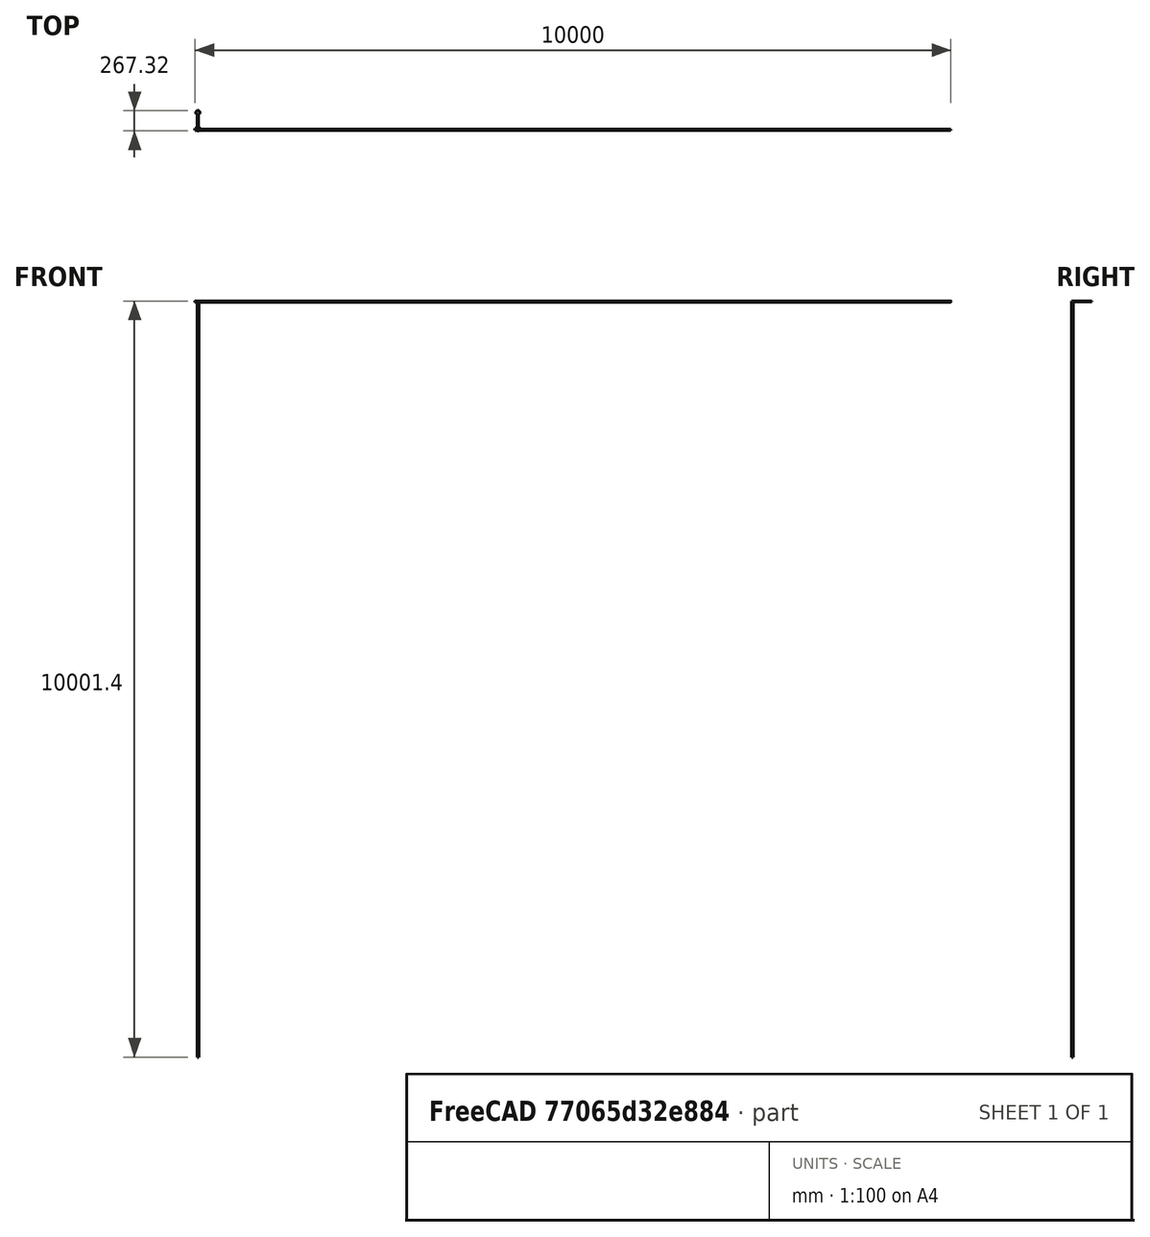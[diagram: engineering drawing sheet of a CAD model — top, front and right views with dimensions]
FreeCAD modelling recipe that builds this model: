
FCSTD DOCUMENT  (FreeCAD 0.16R)
Label: WheelSpacer100mm
License: All rights reserved
LicenseURL: http://en.wikipedia.org/wiki/All_rights_reserved
objects: Sketcher::SketchObject×4, PartDesign::Pocket×3, PartDesign::Chamfer×3, PartDesign::Pad×1, Mesh::Feature×1
note: 15 computed .brp shape members not serialized (recipe doc carries the construction recipe); baked Part::Feature solids carry a one-line shape summary decoded from their .brp

FEATURE [Sketcher::SketchObject] Sketch
  sketch-geometry (9):
    g0: ArcOfCircle CenterX=0 CenterY=227 CenterZ=0 NormalX=0 NormalY=0 NormalZ=1 Radius=25 StartAngle=5.01708 EndAngle=10.6909
    g1: LineSegment [constr] StartX=-40 StartY=252 StartZ=0 EndX=40 EndY=252 EndZ=0
    g2: LineSegment StartX=-7.5 StartY=203.152 StartZ=0 EndX=-7.5 EndY=20 EndZ=0
    g3: LineSegment StartX=7.5 StartY=203.152 StartZ=0 EndX=7.5 EndY=20 EndZ=0
    g4: LineSegment StartX=37.5 StartY=20 StartZ=0 EndX=37.5 EndY=-5 EndZ=0
    g5: LineSegment StartX=37.5 StartY=-5 StartZ=0 EndX=-37.5 EndY=-5 EndZ=0
    g6: LineSegment StartX=-37.5 StartY=-5 StartZ=0 EndX=-37.5 EndY=20 EndZ=0
    g7: LineSegment StartX=-37.5 StartY=20 StartZ=0 EndX=-7.5 EndY=20 EndZ=0
    g8: LineSegment StartX=7.5 StartY=20 StartZ=0 EndX=37.5 EndY=20 EndZ=0
  constraints (28):
    c: Radius(g0) = 25
    c: Tangent(g1,g0)
    c: Horizontal(g1)
    c: Symmetric(g1,g1,g-2)
    c: PointOnObject(g0,g-2)
    c: DistanceY(g1) = 252
    c: Vertical(g2)
    c: Vertical(g3)
    c: Coincident(g4,g5)
    c: Coincident(g5,g6)
    c: Horizontal(g5)
    c: Vertical(g4)
    c: Vertical(g6)
    c: Symmetric(g4,g6,g-2)
    c: Coincident(g7,g6)
    c: Coincident(g7,g2)
    c: Coincident(g8,g3)
    c: Coincident(g8,g4)
    c: Horizontal(g7)
    c: Horizontal(g8)
    c: Distance(g4,g6) = 75
    c: DistanceY(g4) = -5
    c: Coincident(g0,g3)
    c: Coincident(g0,g2)
    c: Symmetric(g0,g0,g-2)
    c: Distance(g0,g0) = 15
    c: DistanceY(g4) = 20
    c: Distance(g1) = 80
FEATURE [PartDesign::Pad] Pad
  Length = 10
  Length2 = 100
  Midplane = true
  Sketch = -> Sketch
  Type = 0
FEATURE [Sketcher::SketchObject] Sketch001
  Placement = pos=(-37.5,0,0) rot=(0.57735,-0.57735,-0.57735;2.0944rad)
  Support = -> Pad [Face5]
  sketch-geometry (1):
    g0: Circle CenterX=0 CenterY=0 CenterZ=0 NormalX=0 NormalY=0 NormalZ=1 Radius=6.35
  constraints (2):
    c: Radius(g0) = 6.35
    c: Coincident(g0,g-1)
FEATURE [PartDesign::Pocket] Pocket
  Length = 5
  Sketch = -> Sketch001
  Type = 1
FEATURE [Sketcher::SketchObject] Sketch002
  Placement = pos=(0,0,5) rot=(0,0,1;0rad)
  Support = -> Pocket [Face5]
  sketch-geometry (3):
    g0: LineSegment StartX=0 StartY=2 StartZ=0 EndX=-10 EndY=-15.3205 EndZ=0
    g1: LineSegment StartX=-10 StartY=-15.3205 StartZ=0 EndX=10 EndY=-15.3205 EndZ=0
    g2: LineSegment StartX=10 StartY=-15.3205 StartZ=0 EndX=0 EndY=2 EndZ=0
  constraints (10):
    c: PointOnObject(g0,g-2)
    c: Coincident(g0,g1)
    c: Horizontal(g1)
    c: Coincident(g1,g2)
    c: Coincident(g2,g0)
    c: DistanceY(g0) = 2
    c: Equal(g2,g0)
    c: Symmetric(g1,g0,g-2)
    c: Distance(g1) = 20
    c: Distance(g2) = 20
FEATURE [PartDesign::Pocket] Pocket001
  Length = 5
  Sketch = -> Sketch002
  Type = 1
FEATURE [Sketcher::SketchObject] Sketch003
  Placement = pos=(0,0,5) rot=(0,0,1;0rad)
  Support = -> Pocket001 [Face5]
  sketch-geometry (3):
    g0: LineSegment StartX=0 StartY=7.0119 StartZ=0 EndX=-10.687 EndY=-5.4526 EndZ=0
    g1: LineSegment StartX=-10.687 StartY=-5.4526 StartZ=0 EndX=10.687 EndY=-5.4526 EndZ=0
    g2: LineSegment StartX=10.687 StartY=-5.4526 StartZ=0 EndX=0 EndY=7.0119 EndZ=0
  constraints (5):
    c: PointOnObject(g0,g-2)
    c: Coincident(g0,g1)
    c: Coincident(g1,g2)
    c: Coincident(g2,g0)
    c: Symmetric(g1,g0,g-2)
FEATURE [PartDesign::Pocket] Pocket002
  Length = 5
  Sketch = -> Sketch003
  Type = 1
FEATURE [PartDesign::Chamfer] Chamfer
  Base = -> Pocket002 [Edge23,Edge20,Edge12,Edge15]
  Size = 0.9
FEATURE [PartDesign::Chamfer] Chamfer001
  Base = -> Chamfer [Edge13,Edge35,Edge37,Edge19]
  Size = 5
FEATURE [PartDesign::Chamfer] Chamfer002
  Base = -> Chamfer001 [Edge45,Edge19]
  Size = 1
FEATURE [Mesh::Feature] Mesh  label="Chamfer002 (Meshed)"
